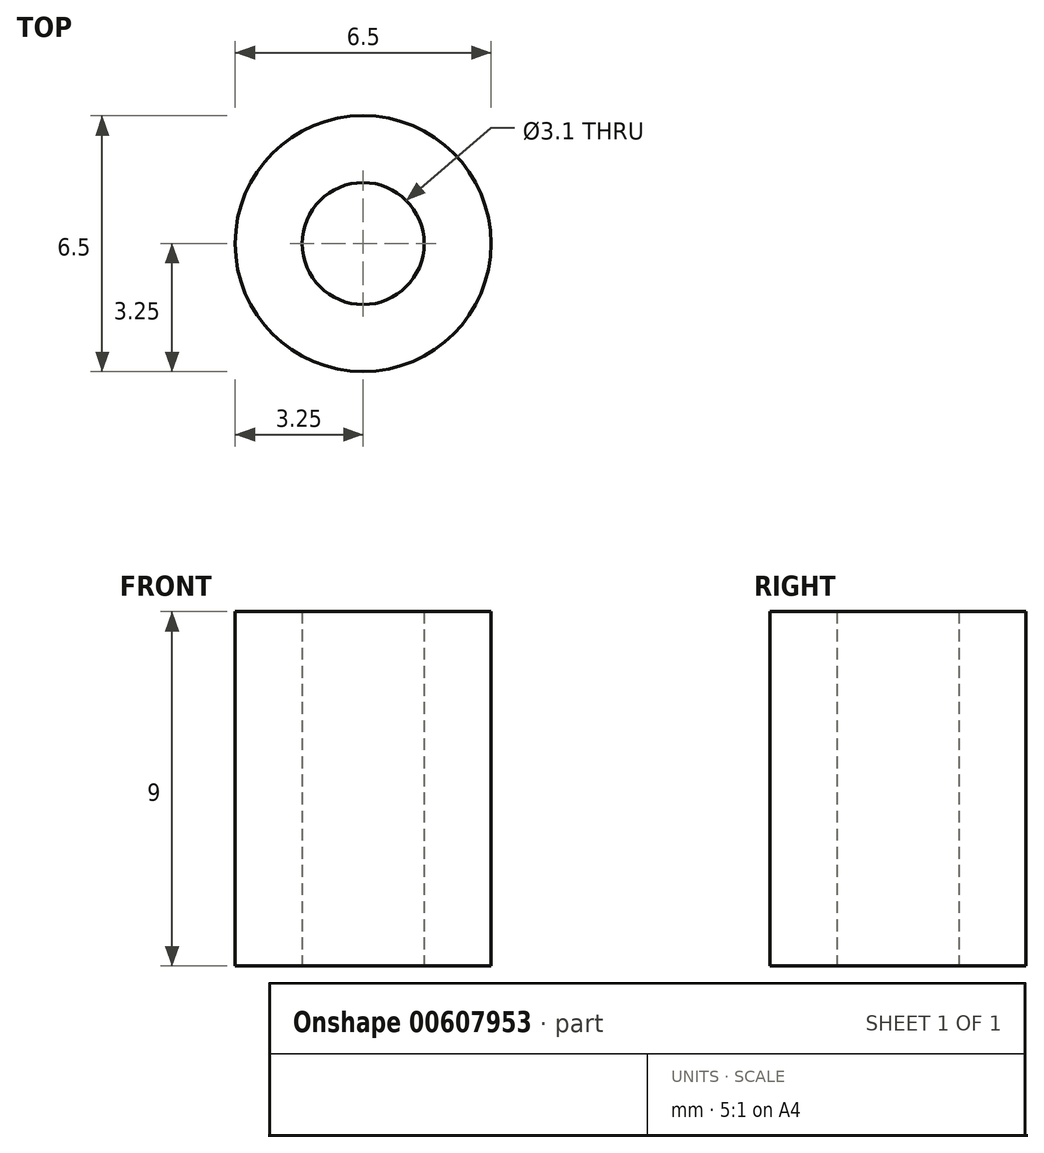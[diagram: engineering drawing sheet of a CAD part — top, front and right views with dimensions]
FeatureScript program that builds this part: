
annotation { "Feature Type Name" : "Feature", "Feature Type Description" : "" }
export const myFeature = defineFeature(function(context is Context, id is Id, definition is map)
    precondition{}
    {
        {
            var Q0;
            Q0=qCreatedBy(makeId("Top.planeOp"),FACE);
            var sketch = newSketch(context, id + "F0", { "sketchPlane" : qUnion([Q0])});
            skCircle(sketch, "E0", {"center": v(0, 0) * mm, "radius": 3.25 * mm});
            skCircle(sketch, "E1", {"center": v(0, 0) * mm, "radius": 1.55 * mm});
            skSolve(sketch);
        }
        {
            var Q0;
            Q0=makeQuery(id+"F0.imprint","IMPRINT",FACE,{"disambiguationData":[TD([[makeQuery(id+"F0.imprint","IMPRINT",EDGE,{"derivedFrom":sQuery(id+"F0.wireOp",EDGE,"E0")}),1.0]])]});
            extrude(context, id + "F1", {"entities" : qUnion([Q0]), "depth" : 9 * mm, "offsetDistance" : 25 * mm});
        }
    });
